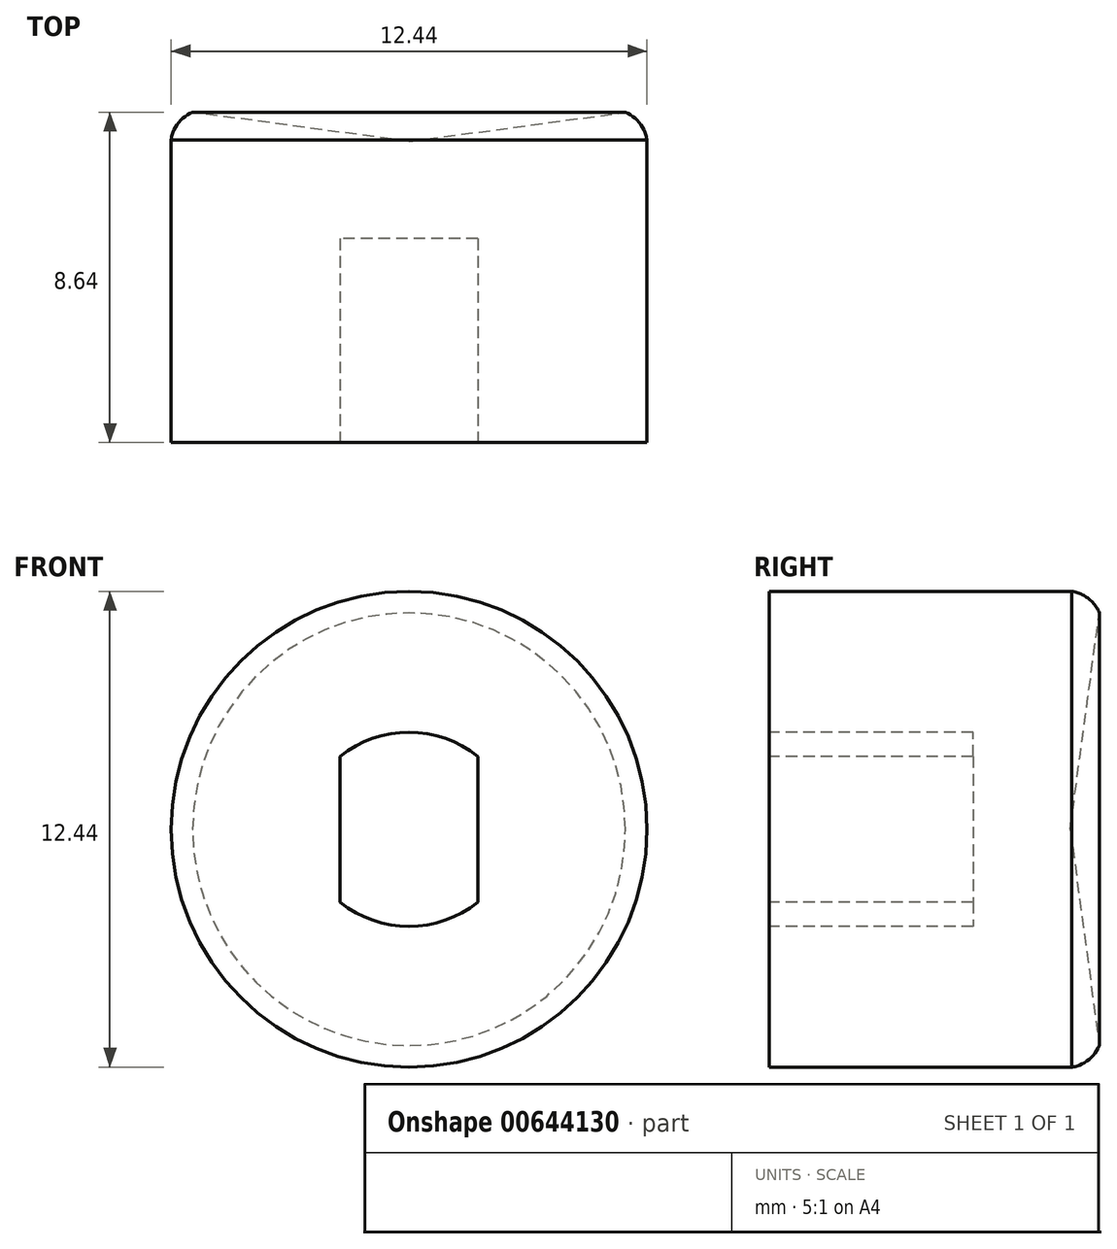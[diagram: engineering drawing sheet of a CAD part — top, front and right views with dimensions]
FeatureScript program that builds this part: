
annotation { "Feature Type Name" : "Feature", "Feature Type Description" : "" }
export const myFeature = defineFeature(function(context is Context, id is Id, definition is map)
    precondition{}
    {
        {
            var Q0;
            Q0=qCreatedBy(makeId("Top.planeOp"),FACE);
            var sketch = newSketch(context, id + "F0", { "sketchPlane" : qUnion([Q0])});
            skLineSegment(sketch, "E0", {"start": v(0, 0) * mm, "end": v(-6.22, 0) * mm});
            skLineSegment(sketch, "E1", {"start": v(0, 7.87) * mm, "end": v(0, 0) * mm});
            skArc(sketch, "E2", {"start": v(-6.22, 7.92) * mm, "mid": v(-6.04, 8.35) * mm, "end": v(-5.66, 8.64) * mm});
            skLineSegment(sketch, "E3", {"start": v(-5.66, 8.64) * mm, "end": v(0, 7.87) * mm});
            skLineSegment(sketch, "E4", {"start": v(-6.22, 7.92) * mm, "end": v(-6.22, 0) * mm});
            skSolve(sketch);
        }
        {
            var Q0;
            Q0 = qSketchRegion(id + "F0", true);
            var Q1;
            Q1=sQuery(id+"F0.wireOp",EDGE,"E1");
            revolve(context, id + "F1", {"entities" : qUnion([Q0]), "axis" : qUnion([Q1]), "revolveType" : RevolveType.ONE_DIRECTION, "angle" : 360 * degree});
        }
        {
            var Q0;
            Q0=qCreatedBy(makeId("Front.planeOp"),FACE);
            var sketch = newSketch(context, id + "F2", { "sketchPlane" : qUnion([Q0])});
            skArc(sketch, "E5", {"start": v(1.8, 1.9) * mm, "mid": v(0, 2.54) * mm, "end": v(-1.8, 1.9) * mm});
            skArc(sketch, "E6", {"start": v(-1.8, -1.9) * mm, "mid": v(0, -2.54) * mm, "end": v(1.8, -1.9) * mm});
            skLineSegment(sketch, "E7", {"start": v(-1.8, 1.9) * mm, "end": v(-1.8, -1.9) * mm});
            skLineSegment(sketch, "E8", {"start": v(1.8, 1.9) * mm, "end": v(1.8, -1.9) * mm});
            skPoint(sketch, "E9", {"position": v(0, 2.54) * mm});
            skPoint(sketch, "E10", {"position": v(0, -2.54) * mm});
            skSolve(sketch);
        }
        {
            var Q0;
            Q0=makeQuery(id+"F2.imprint","IMPRINT",FACE,{"disambiguationData":[TD([[makeQuery(id+"F2.imprint","IMPRINT",EDGE,{"derivedFrom":sQuery(id+"F2.wireOp",EDGE,"E5")}),1.0]])]});
            extrude(context, id + "F3", {"entities" : qUnion([Q0]), "operationType" : NewBodyOperationType.REMOVE, "oppositeDirection" : true, "depth" : 5.33 * mm, "offsetDistance" : 25.4 * mm});
        }
    });
